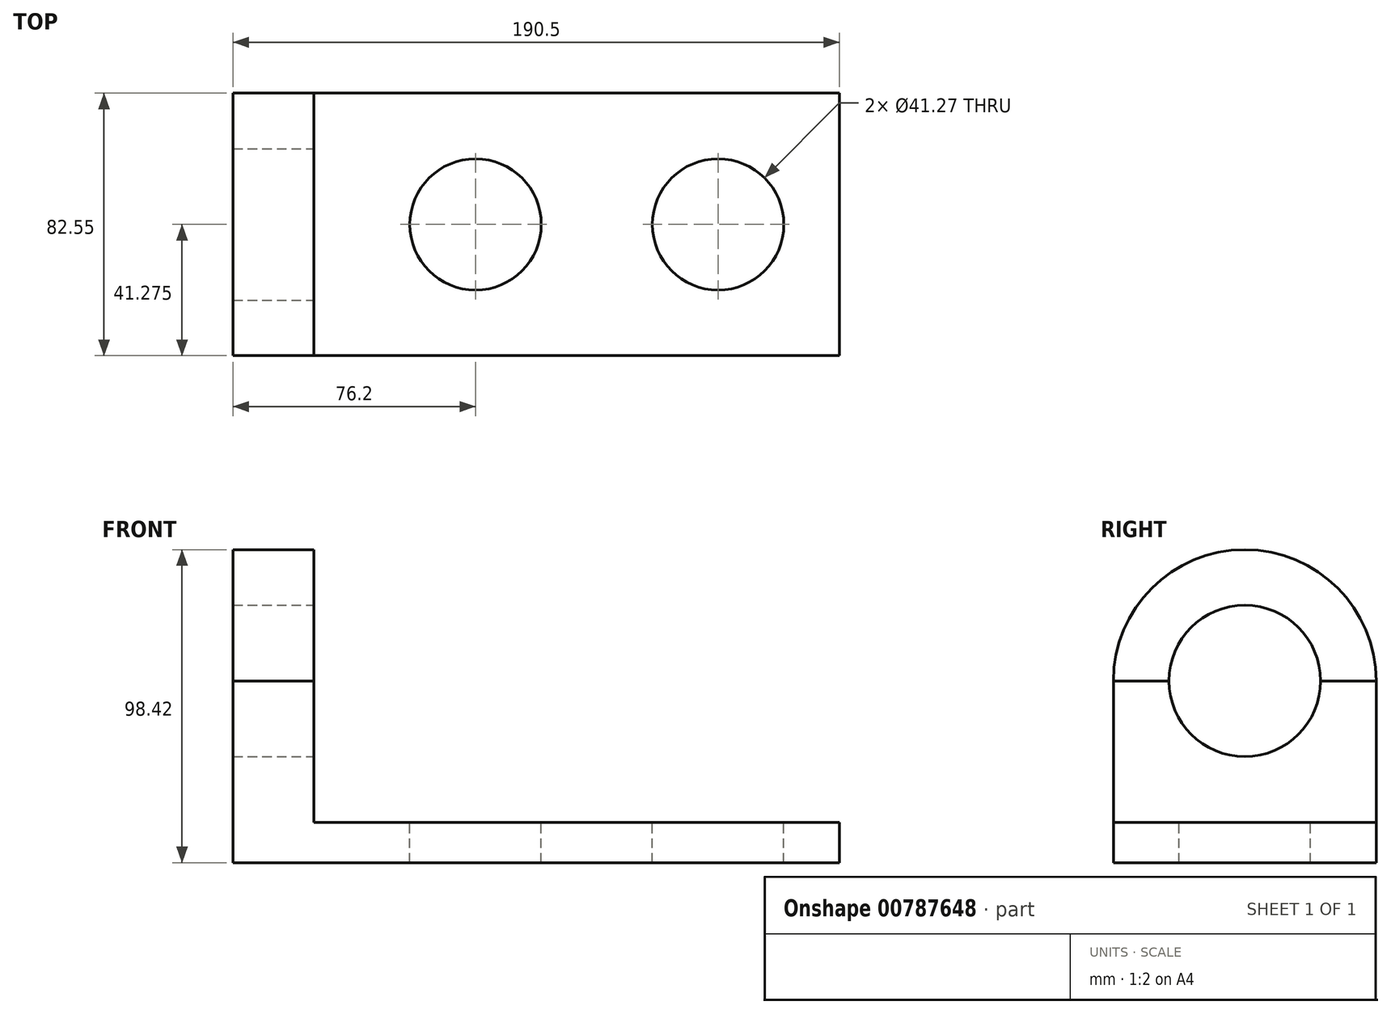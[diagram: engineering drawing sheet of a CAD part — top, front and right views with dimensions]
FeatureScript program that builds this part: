
annotation { "Feature Type Name" : "Feature", "Feature Type Description" : "" }
export const myFeature = defineFeature(function(context is Context, id is Id, definition is map)
    precondition{}
    {
        {
            var Q0;
            Q0=qCreatedBy(makeId("Front.planeOp"),FACE);
            var sketch = newSketch(context, id + "F0", { "sketchPlane" : qUnion([Q0])});
            skLineSegment(sketch, "E0", {"start": v(0, 0) * mm, "end": v(190.5, 0) * mm});
            skLineSegment(sketch, "E1", {"start": v(190.5, 0) * mm, "end": v(190.5, 12.7) * mm});
            skLineSegment(sketch, "E2", {"start": v(190.5, 12.7) * mm, "end": v(25.4, 12.7) * mm});
            skLineSegment(sketch, "E3", {"start": v(25.4, 12.7) * mm, "end": v(25.4, 57.15) * mm});
            skLineSegment(sketch, "E4", {"start": v(25.4, 57.15) * mm, "end": v(0, 57.15) * mm});
            skLineSegment(sketch, "E5", {"start": v(0, 57.15) * mm, "end": v(0, 0) * mm});
            skSolve(sketch);
        }
        {
            var Q0;
            Q0=makeQuery(id+"F0.imprint","IMPRINT",FACE,{"disambiguationData":[TD([[makeQuery(id+"F0.imprint","IMPRINT",EDGE,{"derivedFrom":sQuery(id+"F0.wireOp",EDGE,"E0")}),1.0]])]});
            extrude(context, id + "F1", {"entities" : qUnion([Q0]), "depth" : 82.55 * mm, "offsetDistance" : 25.4 * mm});
        }
        {
            var Q0;
            Q0=makeQuery(id+"F1.opExtrude","SWEPT_FACE",FACE,{"disambiguationData":[OSD([sQuery(id+"F0.wireOp",EDGE,"E2")])]});
            var sketch = newSketch(context, id + "F2", { "sketchPlane" : qUnion([Q0])});
            skLineSegment(sketch, "E6", {"start": v(190.5, -41.28) * mm, "end": v(152.4, -41.28) * mm, "construction": true});
            skLineSegment(sketch, "E7", {"start": v(152.4, -41.28) * mm, "end": v(76.2, -41.28) * mm, "construction": true});
            skCircle(sketch, "E8", {"center": v(76.2, -41.28) * mm, "radius": 20.64 * mm});
            skCircle(sketch, "E9", {"center": v(152.4, -41.28) * mm, "radius": 20.64 * mm});
            skSolve(sketch);
        }
        {
            var Q0;
            Q0=makeQuery(id+"F2.imprint","IMPRINT",FACE,{"disambiguationData":[TD([[makeQuery(id+"F2.imprint","IMPRINT",EDGE,{"derivedFrom":sQuery(id+"F2.wireOp",EDGE,"E8")}),1.0]])]});
            var Q1;
            Q1=makeQuery(id+"F2.imprint","IMPRINT",FACE,{"disambiguationData":[TD([[makeQuery(id+"F2.imprint","IMPRINT",EDGE,{"derivedFrom":sQuery(id+"F2.wireOp",EDGE,"E9")}),1.0]])]});
            extrude(context, id + "F3", {"entities" : qUnion([Q0, Q1]), "operationType" : NewBodyOperationType.REMOVE, "endBound" : BoundingType.THROUGH_ALL, "oppositeDirection" : true, "depth" : 25.4 * mm, "offsetDistance" : 25.4 * mm});
        }
        {
            var Q0;
            Q0=makeQuery(id+"F1.opExtrude","SWEPT_FACE",FACE,{"disambiguationData":[OSD([sQuery(id+"F0.wireOp",EDGE,"E5")])]});
            var sketch = newSketch(context, id + "F4", { "sketchPlane" : qUnion([Q0])});
            skArc(sketch, "E10", {"start": v(82.55, 57.15) * mm, "mid": v(41.28, 98.42) * mm, "end": v(0, 57.15) * mm});
            skSolve(sketch);
        }
        {
            var Q0;
            Q0=makeQuery(id+"F4.imprint","IMPRINT",FACE,{"disambiguationData":[TD([[makeQuery(id+"F4.imprint","IMPRINT",EDGE,{"derivedFrom":sQuery(id+"F4.wireOp",EDGE,"E10")}),1.0]])]});
            extrude(context, id + "F5", {"entities" : qUnion([Q0]), "oppositeDirection" : true, "depth" : 25.4 * mm, "offsetDistance" : 25.4 * mm});
        }
        {
            var Q0;
            Q0=makeQuery(id+"F1.opExtrude","SWEPT_FACE",FACE,{"disambiguationData":[OSD([sQuery(id+"F0.wireOp",EDGE,"E3")])]});
            var sketch = newSketch(context, id + "F6", { "sketchPlane" : qUnion([Q0])});
            skCircle(sketch, "E11", {"center": v(-41.28, 57.15) * mm, "radius": 23.81 * mm});
            skSolve(sketch);
        }
        {
            var Q0;
            {var subQ0=sQuery(id+"F6.wireOp",EDGE,"E11");var subQ1=makeQuery(id+"F1.opExtrude","SWEPT_EDGE",EDGE,{"disambiguationData":[OSD([sQuery(id+"F0.wireOp",EDGE,"E3"),sQuery(id+"F0.wireOp",EDGE,"E4")])]});var subQ2=makeQuery(id+"F6.imprint","INTERSECT",VERTEX,{"disambiguationData":[OD(0.0)],"derivedFrom":[subQ1,subQ0]});Q0=makeQuery(id+"F6.imprint","IMPRINT",FACE,{"disambiguationData":[TD([[makeQuery(id+"F6.imprint","IMPRINT",EDGE,{"disambiguationData":[TD([[subQ2,-1.0]])],"derivedFrom":subQ0}),1.0]])]});}
            extrude(context, id + "F7", {"entities" : qUnion([Q0]), "operationType" : NewBodyOperationType.REMOVE, "oppositeDirection" : true, "depth" : 25.4 * mm, "offsetDistance" : 25.4 * mm});
        }
        {
            var Q0;
            Q0=makeQuery(id+"F1.opExtrude","SWEPT_FACE",FACE,{"disambiguationData":[OSD([sQuery(id+"F0.wireOp",EDGE,"E3")])]});
            var sketch = newSketch(context, id + "F8", { "sketchPlane" : qUnion([Q0])});
            skCircle(sketch, "E12", {"center": v(-41.28, 57.15) * mm, "radius": 23.81 * mm});
            skSolve(sketch);
        }
        {
            var Q0;
            {var subQ0=sQuery(id+"F8.wireOp",EDGE,"E12");var subQ1=makeQuery(id+"F1.opExtrude","SWEPT_EDGE",EDGE,{"disambiguationData":[OSD([sQuery(id+"F0.wireOp",EDGE,"E3"),sQuery(id+"F0.wireOp",EDGE,"E4")])]});var subQ2=makeQuery(id+"F8.imprint","INTERSECT",VERTEX,{"disambiguationData":[OD(0.0)],"derivedFrom":[subQ1,subQ0]});Q0=makeQuery(id+"F8.imprint","IMPRINT",FACE,{"disambiguationData":[TD([[makeQuery(id+"F8.imprint","IMPRINT",EDGE,{"disambiguationData":[TD([[subQ2,1.0]])],"derivedFrom":subQ0}),1.0]])]});}
            extrude(context, id + "F9", {"entities" : qUnion([Q0]), "operationType" : NewBodyOperationType.REMOVE, "oppositeDirection" : true, "depth" : 25.4 * mm, "offsetDistance" : 25.4 * mm});
        }
    });
